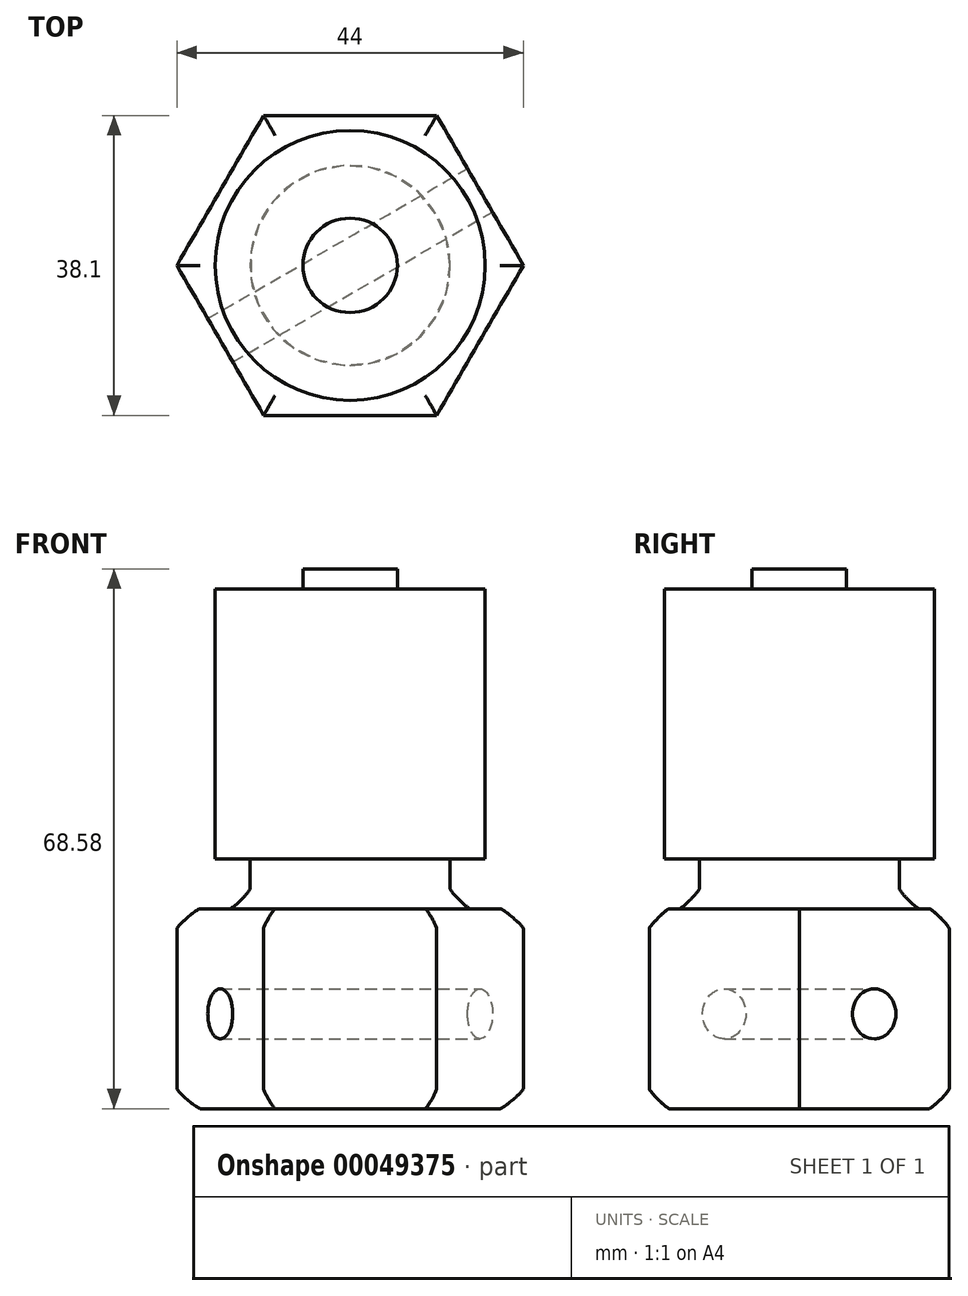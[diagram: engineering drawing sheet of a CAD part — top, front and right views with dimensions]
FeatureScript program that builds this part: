
annotation { "Feature Type Name" : "Feature", "Feature Type Description" : "" }
export const myFeature = defineFeature(function(context is Context, id is Id, definition is map)
    precondition{}
    {
        {
            var Q0;
            Q0=qCreatedBy(makeId("Top.planeOp"),FACE);
            var sketch = newSketch(context, id + "F0", { "sketchPlane" : qUnion([Q0])});
            skCircle(sketch, "E0.cCircle", {"center": v(0, 0) * mm, "radius": 19.05 * mm, "construction": true});
            skLineSegment(sketch, "E0.0", {"start": v(-22, 0) * mm, "end": v(-11, 19.05) * mm});
            skLineSegment(sketch, "E0.1", {"start": v(-11, 19.05) * mm, "end": v(11, 19.05) * mm});
            skLineSegment(sketch, "E0.2", {"start": v(11, 19.05) * mm, "end": v(22, 0) * mm});
            skLineSegment(sketch, "E0.3", {"start": v(22, 0) * mm, "end": v(11, -19.05) * mm});
            skLineSegment(sketch, "E0.4", {"start": v(11, -19.05) * mm, "end": v(-11, -19.05) * mm});
            skLineSegment(sketch, "E0.5", {"start": v(-11, -19.05) * mm, "end": v(-22, 0) * mm});
            skPoint(sketch, "E0.0.midPoint", {"position": v(-16.5, 9.53) * mm});
            skSolve(sketch);
        }
        {
            var Q0;
            Q0 = qSketchRegion(id + "F0", true);
            extrude(context, id + "F1", {"entities" : qUnion([Q0]), "depth" : 25.4 * mm});
        }
        {
            var Q0;
            Q0=makeQuery(id+"F1.opExtrude","CAP_FACE",FACE,{"disambiguationData":[OSD([sQuery(id+"F0.wireOp",EDGE,"E0.0"),sQuery(id+"F0.wireOp",EDGE,"E0.1"),sQuery(id+"F0.wireOp",EDGE,"E0.2"),sQuery(id+"F0.wireOp",EDGE,"E0.3"),sQuery(id+"F0.wireOp",EDGE,"E0.4"),sQuery(id+"F0.wireOp",EDGE,"E0.5")])],"isStart":false});
            var sketch = newSketch(context, id + "F2", { "sketchPlane" : qUnion([Q0])});
            skCircle(sketch, "E1", {"center": v(0, 0) * mm, "radius": 12.7 * mm});
            skSolve(sketch);
        }
        {
            var Q0;
            Q0 = qSketchRegion(id + "F2", true);
            extrude(context, id + "F3", {"entities" : qUnion([Q0]), "operationType" : NewBodyOperationType.ADD, "depth" : 6.35 * mm});
        }
        {
            var Q0;
            Q0=makeQuery(id+"F3.opExtrude","CAP_FACE",FACE,{"disambiguationData":[OSD([sQuery(id+"F2.wireOp",EDGE,"E1")])],"isStart":false});
            var sketch = newSketch(context, id + "F4", { "sketchPlane" : qUnion([Q0])});
            skCircle(sketch, "E2", {"center": v(0, 0) * mm, "radius": 17.15 * mm});
            skSolve(sketch);
        }
        {
            var Q0;
            Q0 = qSketchRegion(id + "F4", true);
            extrude(context, id + "F5", {"entities" : qUnion([Q0]), "operationType" : NewBodyOperationType.ADD, "depth" : 34.3 * mm});
        }
        {
            var Q0;
            Q0=makeQuery(id+"F5.opExtrude","CAP_FACE",FACE,{"disambiguationData":[OSD([sQuery(id+"F4.wireOp",EDGE,"E2")])],"isStart":false});
            var sketch = newSketch(context, id + "F6", { "sketchPlane" : qUnion([Q0])});
            skCircle(sketch, "E3", {"center": v(0, 0) * mm, "radius": 6 * mm});
            skSolve(sketch);
        }
        {
            var Q0;
            Q0 = qSketchRegion(id + "F6", true);
            extrude(context, id + "F7", {"entities" : qUnion([Q0]), "operationType" : NewBodyOperationType.ADD, "depth" : 2.54 * mm});
        }
        {
            var Q0;
            Q0=makeQuery(id+"F1.opExtrude","SWEPT_FACE",FACE,{"disambiguationData":[OSD([sQuery(id+"F0.wireOp",EDGE,"E0.2")])]});
            var sketch = newSketch(context, id + "F8", { "sketchPlane" : qUnion([Q0])});
            skCircle(sketch, "E4", {"center": v(0, 12.05) * mm, "radius": 3.18 * mm});
            skSolve(sketch);
        }
        {
            var Q0;
            Q0 = qSketchRegion(id + "F8", true);
            extrude(context, id + "F9", {"entities" : qUnion([Q0]), "operationType" : NewBodyOperationType.REMOVE, "endBound" : BoundingType.THROUGH_ALL, "oppositeDirection" : true, "depth" : 25.4 * mm});
        }
        {
            var Q0;
            Q0=makeQuery(id+"F1.opExtrude","CAP_FACE",FACE,{"disambiguationData":[OSD([sQuery(id+"F0.wireOp",EDGE,"E0.0"),sQuery(id+"F0.wireOp",EDGE,"E0.1"),sQuery(id+"F0.wireOp",EDGE,"E0.2"),sQuery(id+"F0.wireOp",EDGE,"E0.3"),sQuery(id+"F0.wireOp",EDGE,"E0.4"),sQuery(id+"F0.wireOp",EDGE,"E0.5")])],"isStart":true});
            var Q1;
            Q1=makeQuery(id+"F1.opExtrude","CAP_FACE",FACE,{"disambiguationData":[OSD([sQuery(id+"F0.wireOp",EDGE,"E0.0"),sQuery(id+"F0.wireOp",EDGE,"E0.1"),sQuery(id+"F0.wireOp",EDGE,"E0.2"),sQuery(id+"F0.wireOp",EDGE,"E0.3"),sQuery(id+"F0.wireOp",EDGE,"E0.4"),sQuery(id+"F0.wireOp",EDGE,"E0.5")])],"isStart":false});
            fillet(context, id + "F10", {"entities" : qUnion([Q0, Q1]), "radius" : 2.54 * mm, "tangentPropagation" : true, "rho" : .1, "crossSection" : FilletCrossSection.CONIC, "allowEdgeOverflow" : false});
        }
    });
